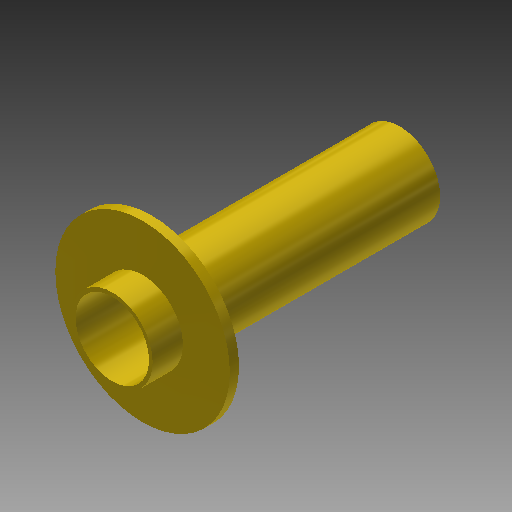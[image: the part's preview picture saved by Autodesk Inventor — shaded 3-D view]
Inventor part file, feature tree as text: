
AUTODESK INVENTOR PART (.ipt)
format: ipt  version: 2017 (Build 210142000, 142)  size: 115,200 bytes
history: native  units: in
note: dims shown in document units (in); Inventor stores cm internally (conversion verified against a paired STEP export)
features: extrude x2, sketch x1
ambient origin geometry x8: Origin, YZ Plane, XZ Plane, XY Plane, X Axis, Y Axis, Z Axis, Center Point
bodies: Solid1 (feature_tree)
feature tree (3):
  sketch  "Sketch1"  dims[d0=1.5748in d1=1.7323in d2=3.7402in d3=2.9528in d4=0.6496in d5=5.5118in d6=0.0in d7=0.0in d8=0.1969in d9=0.0in]
  extrude  "Extrusion1"  Depth=0.1969in
  extrude  "Extrusion2"  Depth=0.1969in
